# Revit family: Door-Slider-Fleetwood-3050-XXXX
name_source: partatom
category: Doors
revit_build: Autodesk Revit 2018 (Build: 20170927_1515(x64)
units: mm (PartAtom-declared; Revit-internal decimal feet)

## family parameters
Always vertical = Yes
Cut with Voids When Loaded = Yes
Host = Wall
OmniClass Number = 23.30.10.00
OmniClass Title = Doors
Room Calculation Point = No
Shared = No

## types (1)
- -
    Actuator_Height = 45.75 "
    Analytic Construction = <None>
    Configuration = XXX
    Exterior Wrap Overhang = 0.5 "
    Frame_&_Panel = Aluminum, Anodized Clear
    Function = Exterior
    Glazing = Glass
    Hardware = Stainless Steel, Brushed
    Height = 96 "
    Interior Wrap Overhang = 0.5 "
    Manufacturer = Fleetwood Windows and Doors
    Model = 4070-T
    Panel_1_Width = 44.5343 "
    Panel_2_Width = 42.6393 "
    Panel_3_Width = 42.6393 "
    Panel_4_Width = 44.5343 "
    Rough Height = 96.25 "
    Rough Width = 170.5 "
    Shim_Space = 0.25 "
    Thickness = 7.632 "
    URL = www.fleetwoodusa.com
    Wall Closure = By host
    Width = 170 "

## geometry (parser evidence)
native form markers: Blend x20, Sweep x25
no freeform markers — native parametric forms only
